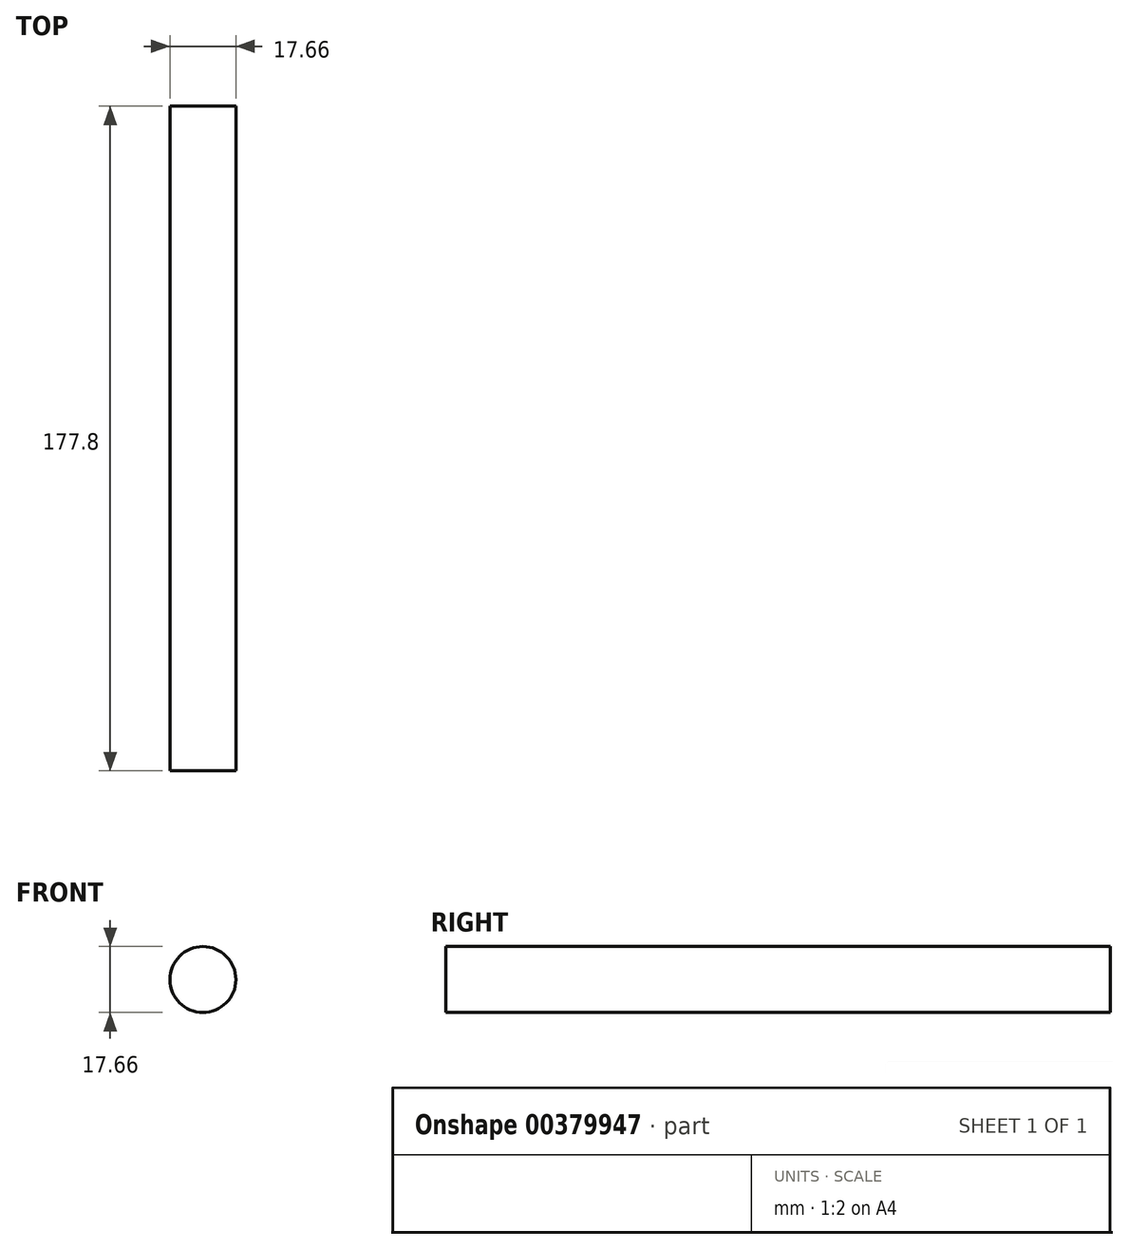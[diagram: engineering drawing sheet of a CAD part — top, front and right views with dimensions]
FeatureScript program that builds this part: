
annotation { "Feature Type Name" : "Feature", "Feature Type Description" : "" }
export const myFeature = defineFeature(function(context is Context, id is Id, definition is map)
    precondition{}
    {
        {
            var Q0;
            Q0=qCreatedBy(makeId("Front.planeOp"),FACE);
            var sketch = newSketch(context, id + "F0", { "sketchPlane" : qUnion([Q0])});
            skCircle(sketch, "E0", {"center": v(0, 0) * mm, "radius": 8.83 * mm});
            skSolve(sketch);
        }
        {
            var Q0;
            Q0=makeQuery(id+"F0.imprint","IMPRINT",FACE,{"disambiguationData":[TD([[makeQuery(id+"F0.imprint","IMPRINT",EDGE,{"derivedFrom":sQuery(id+"F0.wireOp",EDGE,"E0")}),1.0]])]});
            extrude(context, id + "F1", {"entities" : qUnion([Q0]), "oppositeDirection" : true, "depth" : 177.8 * mm});
        }
    });
